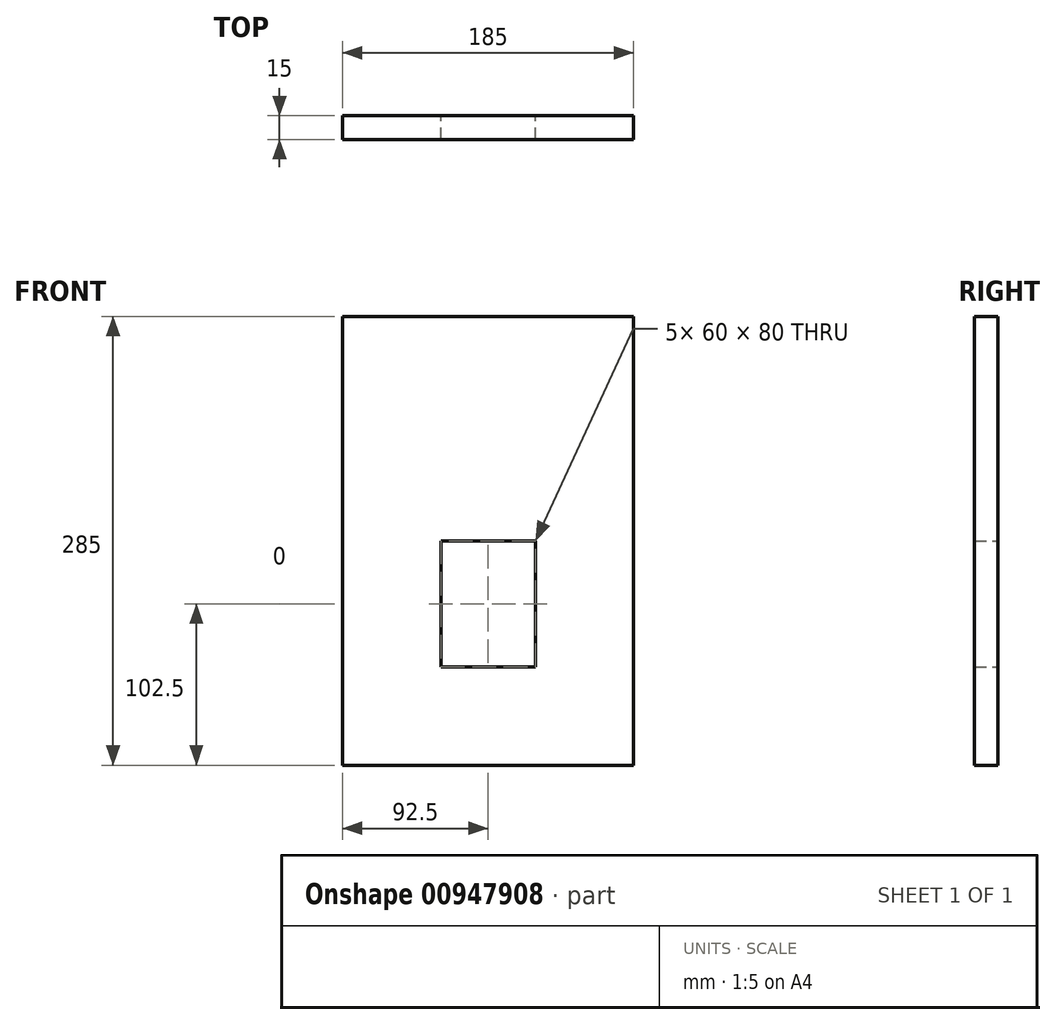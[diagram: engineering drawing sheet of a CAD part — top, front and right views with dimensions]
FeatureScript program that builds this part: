
annotation { "Feature Type Name" : "Feature", "Feature Type Description" : "" }
export const myFeature = defineFeature(function(context is Context, id is Id, definition is map)
    precondition{}
    {
        {
            var Q0;
            Q0=qCreatedBy(makeId("Right.planeOp"),FACE);
            cPlane(context, id + "F0", {"entities" : qUnion([Q0]), "cplaneType" : CPlaneType.OFFSET, "offset" : (100 - 7.5) * mm, "width" : 150 * mm, "height" : 150 * mm});
        }
        {
            var Q0;
            Q0=qCreatedBy(makeId("Right.planeOp"),FACE);
            cPlane(context, id + "F1", {"entities" : qUnion([Q0]), "cplaneType" : CPlaneType.OFFSET, "offset" : 92.5 * mm, "oppositeDirection" : true, "width" : 150 * mm, "height" : 150 * mm});
        }
        {
            var Q0;
            Q0=qCreatedBy(makeId("Top.planeOp"),FACE);
            cPlane(context, id + "F2", {"entities" : qUnion([Q0]), "cplaneType" : CPlaneType.OFFSET, "offset" : 7.5 * mm, "width" : 150 * mm, "height" : 150 * mm});
        }
        {
            var Q0;
            Q0=qCreatedBy(makeId("Top.planeOp"),FACE);
            cPlane(context, id + "F3", {"entities" : qUnion([Q0]), "cplaneType" : CPlaneType.OFFSET, "offset" : (300 - 7.5) * mm, "width" : 150 * mm, "height" : 150 * mm});
        }
        {
            var Q0;
            Q0=qCreatedBy(makeId("Front.planeOp"),FACE);
            cPlane(context, id + "F4", {"entities" : qUnion([Q0]), "cplaneType" : CPlaneType.OFFSET, "offset" : 150 * mm, "oppositeDirection" : true, "width" : 150 * mm, "height" : 150 * mm});
        }
        {
            var Q0;
            Q0=qCreatedBy(makeId("Front.planeOp"),FACE);
            cPlane(context, id + "F5", {"entities" : qUnion([Q0]), "cplaneType" : CPlaneType.OFFSET, "offset" : (150 - 15) * mm, "oppositeDirection" : true, "width" : 150 * mm, "height" : 150 * mm});
        }
        {
            var Q0;
            Q0=qCreatedBy(id+"F4.planeOp",FACE);
            var sketch = newSketch(context, id + "F6", { "sketchPlane" : qUnion([Q0])});
            skLineSegment(sketch, "E0.bottom", {"start": v(-92.5, 292.5) * mm, "end": v(92.5, 292.5) * mm});
            skLineSegment(sketch, "E0.top", {"start": v(-92.5, 7.5) * mm, "end": v(92.5, 7.5) * mm});
            skLineSegment(sketch, "E0.left", {"start": v(-92.5, 292.5) * mm, "end": v(-92.5, 7.5) * mm});
            skLineSegment(sketch, "E0.right", {"start": v(92.5, 292.5) * mm, "end": v(92.5, 7.5) * mm});
            skSolve(sketch);
        }
        {
            var Q0;
            Q0 = qSketchRegion(id + "F6", true);
            var Q1;
            Q1=qCreatedBy(id+"F5.planeOp",FACE);
            extrude(context, id + "F7", {"entities" : qUnion([Q0]), "endBound" : BoundingType.UP_TO_SURFACE, "depth" : 25 * mm, "endBoundEntityFace" : qUnion([Q1]), "offsetDistance" : 25 * mm});
        }
        {
            var Q0;
            Q0=qCreatedBy(id+"F4.planeOp",FACE);
            var sketch = newSketch(context, id + "F8", { "sketchPlane" : qUnion([Q0])});
            skLineSegment(sketch, "E1.bottom", {"start": v(30, 150) * mm, "end": v(-30, 150) * mm});
            skLineSegment(sketch, "E1.top", {"start": v(30, 70) * mm, "end": v(-30, 70) * mm});
            skLineSegment(sketch, "E1.left", {"start": v(30, 150) * mm, "end": v(30, 70) * mm});
            skLineSegment(sketch, "E1.right", {"start": v(-30, 150) * mm, "end": v(-30, 70) * mm});
            skSolve(sketch);
        }
        {
            var Q0;
            Q0 = qSketchRegion(id + "F8", true);
            var Q1;
            Q1=qCreatedBy(id+"F5.planeOp",FACE);
            extrude(context, id + "F9", {"entities" : qUnion([Q0]), "operationType" : NewBodyOperationType.REMOVE, "endBound" : BoundingType.UP_TO_SURFACE, "depth" : 25 * mm, "endBoundEntityFace" : qUnion([Q1]), "offsetDistance" : 25 * mm});
        }
    });
